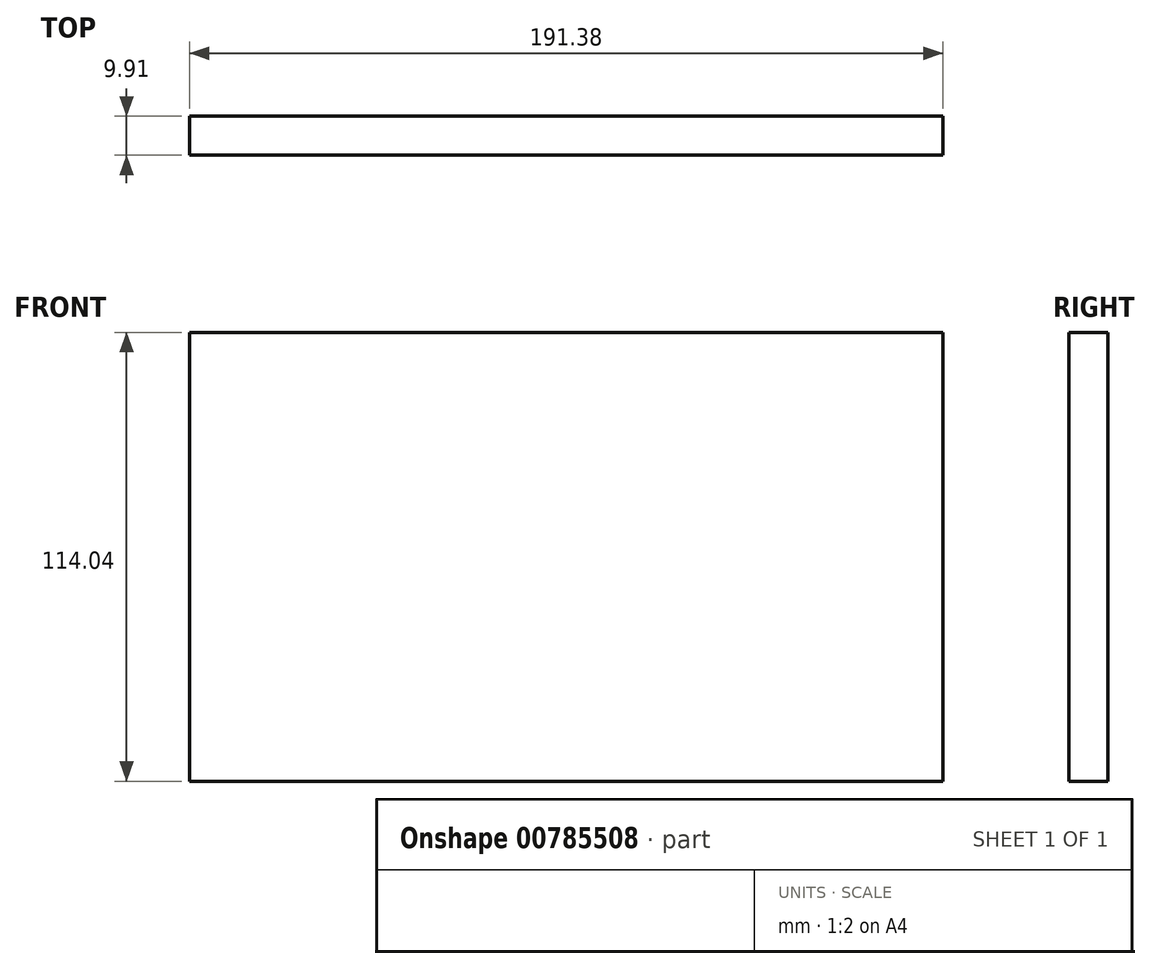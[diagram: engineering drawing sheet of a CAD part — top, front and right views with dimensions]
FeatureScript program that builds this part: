
annotation { "Feature Type Name" : "Feature", "Feature Type Description" : "" }
export const myFeature = defineFeature(function(context is Context, id is Id, definition is map)
    precondition{}
    {
        {
            var Q0;
            Q0=qCreatedBy(makeId("Front.planeOp"),FACE);
            var sketch = newSketch(context, id + "F0", { "sketchPlane" : qUnion([Q0])});
            skLineSegment(sketch, "E0.bottom", {"start": v(95.7, 57.02) * mm, "end": v(-95.7, 57.02) * mm});
            skLineSegment(sketch, "E0.top", {"start": v(95.7, -57.02) * mm, "end": v(-95.7, -57.02) * mm});
            skLineSegment(sketch, "E0.left", {"start": v(95.7, 57.02) * mm, "end": v(95.7, -57.02) * mm});
            skLineSegment(sketch, "E0.right", {"start": v(-95.7, 57.02) * mm, "end": v(-95.7, -57.02) * mm});
            skPoint(sketch, "E0.middle", {"position": v(0, 0) * mm});
            skSolve(sketch);
        }
        {
            var Q0;
            Q0 = qSketchRegion(id + "F0", true);
            extrude(context, id + "F1", {"entities" : qUnion([Q0]), "depth" : 9.9 * mm, "offsetDistance" : 25.4 * mm});
        }
    });
